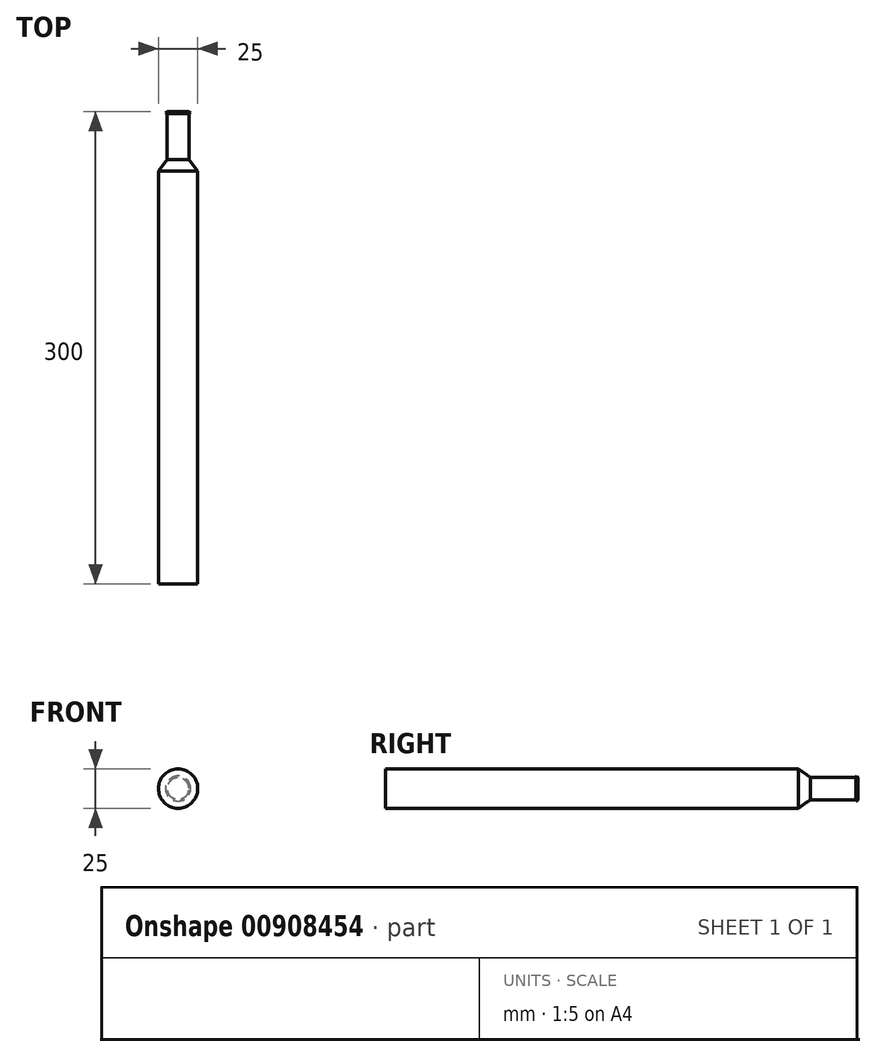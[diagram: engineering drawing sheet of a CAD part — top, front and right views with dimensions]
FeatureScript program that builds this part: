
annotation { "Feature Type Name" : "Feature", "Feature Type Description" : "" }
export const myFeature = defineFeature(function(context is Context, id is Id, definition is map)
    precondition{}
    {
        {
            var Q0;
            Q0=qCreatedBy(makeId("Front.planeOp"),FACE);
            var sketch = newSketch(context, id + "F0", { "sketchPlane" : qUnion([Q0])});
            skCircle(sketch, "E0", {"center": v(0, 0) * mm, "radius": 12.5 * mm});
            skSolve(sketch);
        }
        {
            var Q0;
            Q0 = qSketchRegion(id + "F0", true);
            extrude(context, id + "F1", {"entities" : qUnion([Q0]), "depth" : 300 * mm, "offsetDistance" : 25 * mm});
        }
        {
            var Q0;
            Q0=qCreatedBy(makeId("Top.planeOp"),FACE);
            var sketch = newSketch(context, id + "F2", { "sketchPlane" : qUnion([Q0])});
            skLineSegment(sketch, "E1", {"start": v(0, 0) * mm, "end": v(0, -2) * mm});
            skLineSegment(sketch, "E2", {"start": v(-8, -0.65) * mm, "end": v(-6.87, 0) * mm});
            skLineSegment(sketch, "E3", {"start": v(-7, -1.23) * mm, "end": v(-7, -30.29) * mm});
            skPoint(sketch, "E4.orphan", {"position": v(-7, -4) * mm});
            skLineSegment(sketch, "E5", {"start": v(-7, -30.29) * mm, "end": v(-14.2, -40.11) * mm});
            skLineSegment(sketch, "E6", {"start": v(-14.2, -40.11) * mm, "end": v(-14.2, 3.67) * mm});
            skLineSegment(sketch, "E7", {"start": v(-8, -0.65) * mm, "end": v(-4.36, -0.65) * mm});
            skLineSegment(sketch, "E8", {"start": v(-8, -0.65) * mm, "end": v(-7, -1.23) * mm});
            skLineSegment(sketch, "E9", {"start": v(-14.2, 3.67) * mm, "end": v(-6.87, 0) * mm});
            skSolve(sketch);
        }
        {
            var Q0;
            Q0 = qSketchRegion(id + "F2", true);
            var Q1;
            Q1=sQuery(id+"F2.wireOp",EDGE,"E1");
            revolve(context, id + "F3", {"operationType" : NewBodyOperationType.REMOVE, "surfaceOperationType" : NewSurfaceOperationType.NEW, "entities" : qUnion([Q0]), "axis" : qUnion([Q1]), "revolveType" : RevolveType.FULL, "oppositeDirection" : true});
        }
    });
